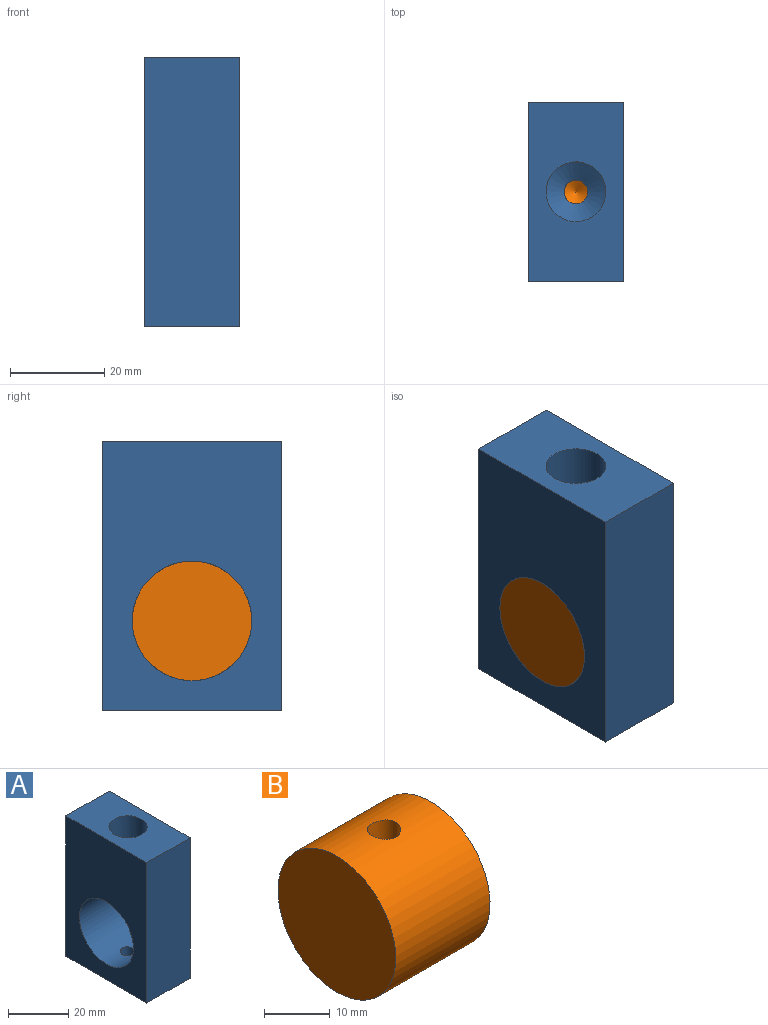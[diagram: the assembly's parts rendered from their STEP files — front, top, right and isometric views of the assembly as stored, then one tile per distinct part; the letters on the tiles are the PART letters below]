
ASSEMBLY  parts=2 mates=1
PART A: 11 faces, bbox 20.3x38.1x57.2 mm
  f0: cylinder r=2.54mm len=5.08mm, axis (0,0,1), area 66.9mm2, adj f7,f9
  f1: plane 57.15x38.1mm, normal (-1,0,0), area 1670.7mm2, adj f2,f4,f5,f6,f7
  f2: plane 38.1x20.32mm, normal (0,0,-1), area 753.9mm2, adj f1,f3,f5,f6,f8
  f3: plane 57.15x38.1mm, normal (1,0,0), area 1670.7mm2, adj f2,f4,f5,f6,f7
  f4: plane 38.1x20.32mm, normal (0,0,1), area 647.5mm2, adj f1,f3,f5,f6,f10
  f5: plane 57.15x20.32mm, normal (0,-1,0), area 1161.3mm2, adj f1,f2,f3,f4
  f6: plane 57.15x20.32mm, normal (0,1,0), area 1161.3mm2, adj f1,f2,f3,f4
  f7: cylinder r=12.7mm len=25.4mm, axis (1,0,0), area 1580.8mm2, adj f0,f1,f3,f8
  f8: cylinder r=2.54mm len=6.61mm, axis (0,0,1), area 103.4mm2, adj f2,f7
  f9: cone r=0mm half-angle=59deg, axis (0,0,1), area 124.1mm2, adj f0,f10
  f10: cylinder r=6.35mm len=19.05mm, axis (0,0,1), area 760.1mm2, adj f4,f9
PART B: 7 faces, bbox 20.3x25.4x25.4 mm
  f0: cylinder r=12.7mm len=25.4mm, axis (-1,0,0), area 1580.6mm2, adj f1,f2,f3,f5
  f1: plane 25.4x25.4mm, normal (1,0,0), area 506.7mm2, adj f0
  f2: plane 25.4x25.4mm, normal (-1,0,0), area 506.7mm2, adj f0
  f3: cylinder r=2.54mm len=7.88mm, axis (0,0,1), area 123.7mm2, adj f0,f4
  f4: cone r=0mm half-angle=59deg, axis (0,0,1), area 23.6mm2, adj f3
  f5: cylinder r=2.54mm len=7.88mm, axis (0,0,-1), area 123.7mm2, adj f0,f6
  f6: cone r=0mm half-angle=59deg, axis (0,0,-1), area 23.6mm2, adj f5
PLACE A t=(-18.77,-1.22,5.63)mm
PLACE B t=(-18.77,-1.22,24.68)mm
MATE revolute B.f0 <-> A.f7  axis (-1,0,0) through (-8.61,-1.22,24.68)mm
